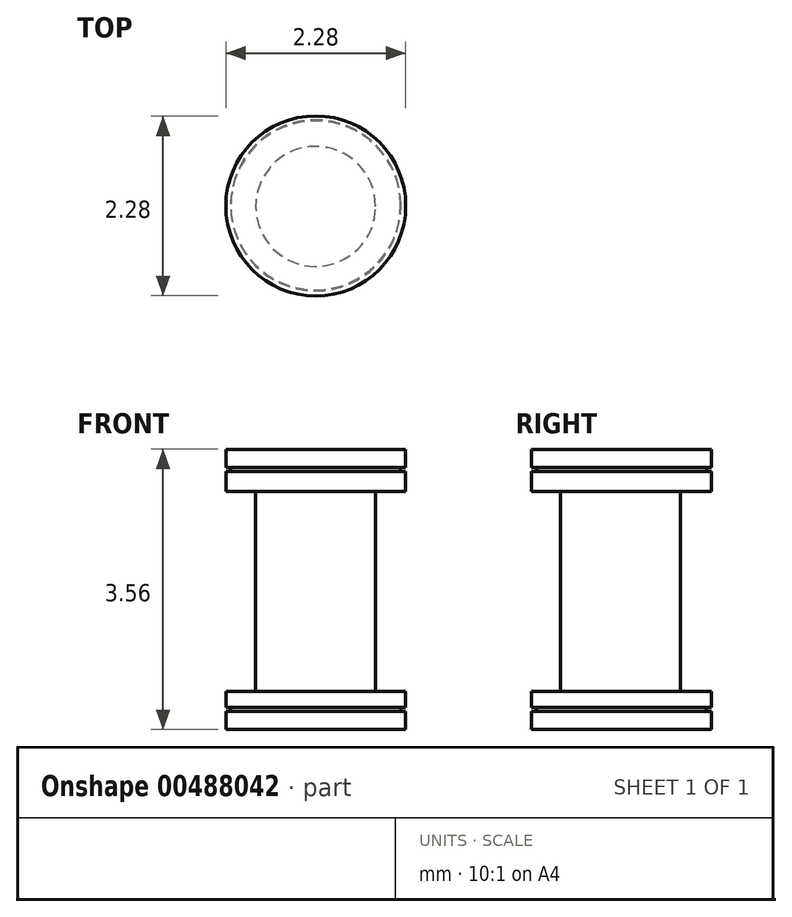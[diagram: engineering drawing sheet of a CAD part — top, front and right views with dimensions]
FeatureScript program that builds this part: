
annotation { "Feature Type Name" : "Feature", "Feature Type Description" : "" }
export const myFeature = defineFeature(function(context is Context, id is Id, definition is map)
    precondition{}
    {
        {
            var Q0;
            Q0=qCreatedBy(makeId("Top.planeOp"),FACE);
            var sketch = newSketch(context, id + "F0", { "sketchPlane" : qUnion([Q0])});
            skCircle(sketch, "E0", {"center": v(0, 0) * mm, "radius": 1.14 * mm});
            skSolve(sketch);
        }
        {
            var Q0;
            Q0=qSketchRegion(id+"F0",true);
            extrude(context, id + "F1", {"entities" : qUnion([Q0]), "depth" : 3.56 * mm, "offsetDistance" : 25.4 * mm});
        }
        {
            var Q0;
            Q0=qCreatedBy(makeId("Top.planeOp"),FACE);
            cPlane(context, id + "F2", {"entities" : qUnion([Q0]), "cplaneType" : CPlaneType.OFFSET, "offset" : 0.23 * mm, "width" : 152.4 * mm, "height" : 152.4 * mm});
        }
        {
            var Q0;
            Q0=qCreatedBy(id+"F2.planeOp",FACE);
            cPlane(context, id + "F3", {"entities" : qUnion([Q0]), "cplaneType" : CPlaneType.OFFSET, "offset" : 3.1 * mm, "width" : 152.4 * mm, "height" : 152.4 * mm});
        }
        {
            var Q0;
            Q0=qCreatedBy(id+"F2.planeOp",FACE);
            var sketch = newSketch(context, id + "F4", { "sketchPlane" : qUnion([Q0])});
            skCircle(sketch, "E1", {"center": v(0, 0) * mm, "radius": 1.08 * mm});
            skCircle(sketch, "E2", {"center": v(0, 0) * mm, "radius": 1.14 * mm});
            skSolve(sketch);
        }
        {
            var Q0;
            Q0=qSketchRegion(id+"F4",true);
            extrude(context, id + "F5", {"entities" : qUnion([Q0]), "operationType" : NewBodyOperationType.REMOVE, "depth" : 0.05 * mm, "offsetDistance" : 25.4 * mm});
        }
        {
            var Q0;
            Q0=qCreatedBy(id+"F3.planeOp",FACE);
            var sketch = newSketch(context, id + "F6", { "sketchPlane" : qUnion([Q0])});
            skCircle(sketch, "E3", {"center": v(0, 0.01) * mm, "radius": 1.08 * mm});
            skCircle(sketch, "E4", {"center": v(0, 0.01) * mm, "radius": 1.16 * mm});
            skSolve(sketch);
        }
        {
            var Q0;
            Q0=qSketchRegion(id+"F6",true);
            var Q1;
            Q1=qConstructionFilter(qBodyType(qCreatedBy(id+"F6",EDGE),BodyType.WIRE),ConstructionObject.NO);
            extrude(context, id + "F7", {"entities" : qUnion([Q0]), "operationType" : NewBodyOperationType.REMOVE, "surfaceEntities" : qUnion([Q1]), "oppositeDirection" : true, "depth" : 0.05 * mm, "offsetDistance" : 25.4 * mm});
        }
        {
            var Q0;
            Q0=qCreatedBy(id+"F2.planeOp",FACE);
            cPlane(context, id + "F8", {"entities" : qUnion([Q0]), "cplaneType" : CPlaneType.OFFSET, "offset" : 0.25 * mm, "width" : 152.4 * mm, "height" : 152.4 * mm});
        }
        {
            var Q0;
            Q0=qCreatedBy(id+"F8.planeOp",FACE);
            var sketch = newSketch(context, id + "F9", { "sketchPlane" : qUnion([Q0])});
            skCircle(sketch, "E5", {"center": v(0, 0) * mm, "radius": 0.76 * mm});
            skCircle(sketch, "E6", {"center": v(0, 0) * mm, "radius": 1.16 * mm});
            skSolve(sketch);
        }
        {
            var Q0;
            Q0 = qSketchRegion(id + "F9", true);
            var Q1;
            Q1 = qConstructionFilter(qBodyType(qCreatedBy(id + "F9" ,EDGE), BodyType.WIRE), ConstructionObject.NO);
            extrude(context, id + "F10", {"entities" : qUnion([Q0]), "operationType" : NewBodyOperationType.REMOVE, "surfaceEntities" : qUnion([Q1]), "depth" : 2.54 * mm, "offsetDistance" : 25.4 * mm});
        }
    });
